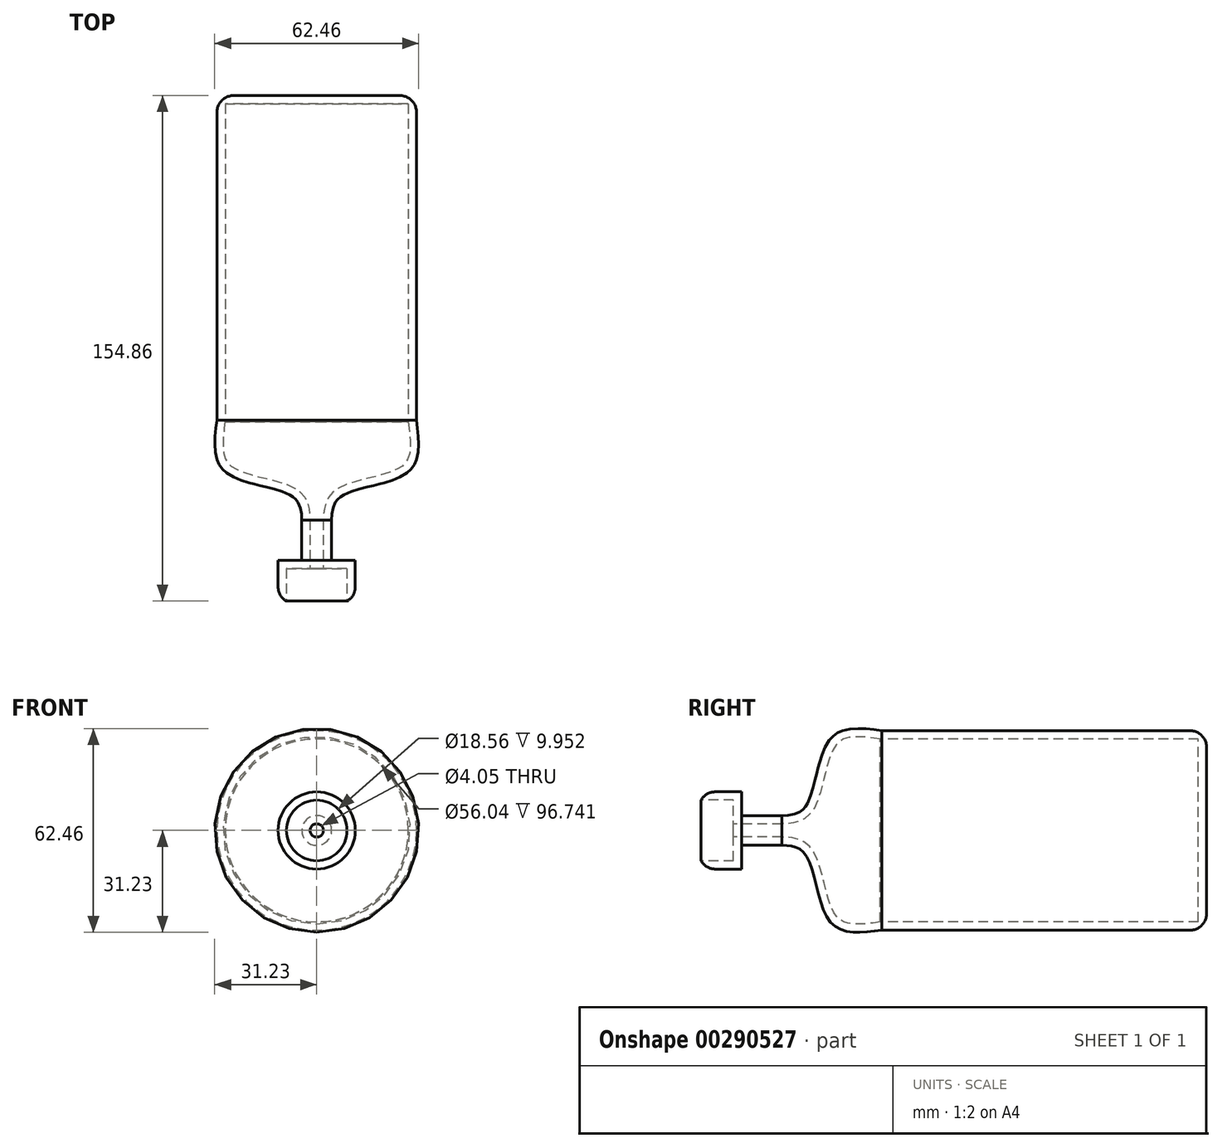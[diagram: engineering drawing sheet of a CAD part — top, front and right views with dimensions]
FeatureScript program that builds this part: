
annotation { "Feature Type Name" : "Feature", "Feature Type Description" : "" }
export const myFeature = defineFeature(function(context is Context, id is Id, definition is map)
    precondition{}
    {
        {
            var Q0;
            Q0=qCreatedBy(makeId("Top.planeOp"),FACE);
            var sketch = newSketch(context, id + "F0", { "sketchPlane" : qUnion([Q0])});
            skLineSegment(sketch, "E0", {"start": v(0, 0) * mm, "end": v(30.56, 0) * mm});
            skLineSegment(sketch, "E1", {"start": v(30.56, 0) * mm, "end": v(30.56, -99.45) * mm});
            skFitSpline(sketch, "E2", {"points": [v(30.56, -99.45) * mm, v(28.14, -115.17) * mm, v(7.39, -122.82) * mm, v(4.57, -130.08) * mm], "startDerivative": vector(7.07, -52.78) * mm, "endDerivative": vector(-1.26, -33.58) * mm});
            skLineSegment(sketch, "E3", {"start": v(4.57, -130.08) * mm, "end": v(4.57, -142.37) * mm});
            skLineSegment(sketch, "E4", {"start": v(4.57, -142.37) * mm, "end": v(11.82, -142.37) * mm});
            skLineSegment(sketch, "E5", {"start": v(11.82, -142.37) * mm, "end": v(11.82, -154.86) * mm});
            skLineSegment(sketch, "E6", {"start": v(11.82, -154.86) * mm, "end": v(0, -154.86) * mm});
            skLineSegment(sketch, "E7", {"start": v(0, -154.86) * mm, "end": v(0, 0) * mm});
            skLineSegment(sketch, "E8", {"start": v(0, -66) * mm, "end": v(0, 31.71) * mm, "construction": true});
            skSolve(sketch);
        }
        {
            var Q0;
            Q0=makeQuery(id+"F0.imprint","IMPRINT",FACE,{"disambiguationData":[TD([[makeQuery(id+"F0.imprint","IMPRINT",EDGE,{"derivedFrom":sQuery(id+"F0.wireOp",EDGE,"E0")}),-1.0]])]});
            var Q1;
            Q1=sQuery(id+"F0.wireOp",EDGE,"E8");
            revolve(context, id + "F1", {"entities" : qUnion([Q0]), "axis" : qUnion([Q1]), "revolveType" : RevolveType.FULL});
        }
        {
            var Q0;
            Q0=makeQuery(id+"F1.opRevolve","SWEPT_FACE",FACE,{"disambiguationData":[OSD([sQuery(id+"F0.wireOp",EDGE,"E6")])]});
            shell(context, id + "F2", {"entities" : qUnion([Q0]), "thickness" : 2.54 * mm});
        }
        {
            var Q0;
            Q0=makeQuery(id+"F1.opRevolve","SWEPT_EDGE",EDGE,{"disambiguationData":[OSD([sQuery(id+"F0.wireOp",EDGE,"E5"),sQuery(id+"F0.wireOp",EDGE,"E6")])]});
            fillet(context, id + "F3", {"entities" : qUnion([Q0]), "radius" : 5.08 * mm, "tangentPropagation" : true, "allowEdgeOverflow" : false});
        }
        {
            var Q0;
            Q0=makeQuery(id+"F1.opRevolve","SWEPT_EDGE",EDGE,{"disambiguationData":[OSD([sQuery(id+"F0.wireOp",EDGE,"E0"),sQuery(id+"F0.wireOp",EDGE,"E1")])]});
            fillet(context, id + "F4", {"entities" : qUnion([Q0]), "radius" : 5.08 * mm, "tangentPropagation" : true, "allowEdgeOverflow" : false});
        }
        {
            var Q0;
            Q0=makeQuery(id+"F2.opShell","OFFSET_EDGE",EDGE,{"disambiguationData":[OSD([sQuery(id+"F0.wireOp",EDGE,"E1"),sQuery(id+"F0.wireOp",EDGE,"E2")])]});
            chamfer(context, id + "F5", {"entities" : qUnion([Q0]), "width" : 5.08 * mm, "tangentPropagation" : true});
        }
    });
